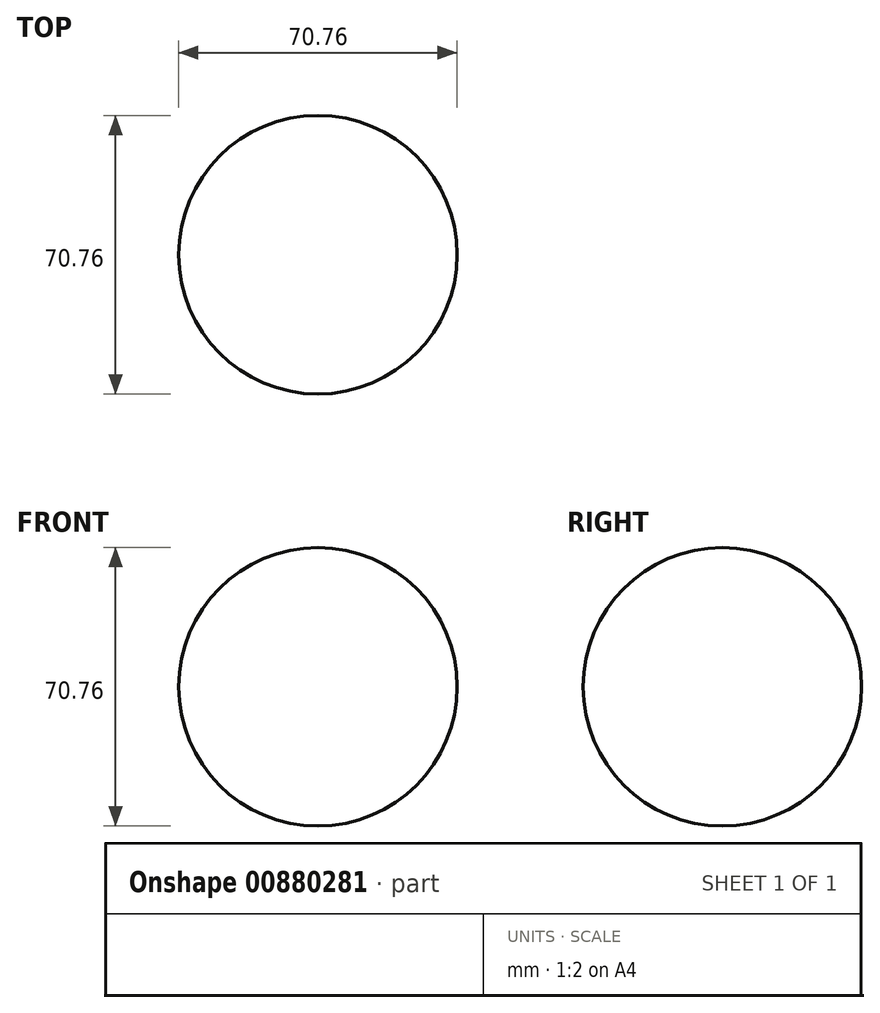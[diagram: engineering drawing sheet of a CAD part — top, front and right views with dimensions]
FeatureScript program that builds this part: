
annotation { "Feature Type Name" : "Feature", "Feature Type Description" : "" }
export const myFeature = defineFeature(function(context is Context, id is Id, definition is map)
    precondition{}
    {
        {
            var Q0;
            Q0=qCreatedBy(makeId("Top.planeOp"),FACE);
            var sketch = newSketch(context, id + "F0", { "sketchPlane" : qUnion([Q0])});
            skArc(sketch, "E0", {"start": v(35.38, 0) * mm, "mid": v(0, 35.38) * mm, "end": v(-35.38, 0) * mm});
            skLineSegment(sketch, "E1", {"start": v(0, 0) * mm, "end": v(35.38, 0) * mm});
            skLineSegment(sketch, "E2", {"start": v(35.38, 0) * mm, "end": v(-35.38, 0) * mm});
            skSolve(sketch);
        }
        {
            var Q0;
            {var subQ0=sQuery(id+"F0.wireOp",EDGE,"E0");Q0=makeQuery(id+"F0.imprint","IMPRINT",FACE,{"disambiguationData":[TD([[makeQuery(id+"F0.imprint","IMPRINT",EDGE,{"derivedFrom":subQ0}),1.0]])]});}
            var Q1;
            Q1=sQuery(id+"F0.wireOp",EDGE,"E2");
            revolve(context, id + "F1", {"surfaceOperationType" : NewSurfaceOperationType.NEW, "entities" : qUnion([Q0]), "axis" : qUnion([Q1]), "revolveType" : RevolveType.FULL});
        }
    });
